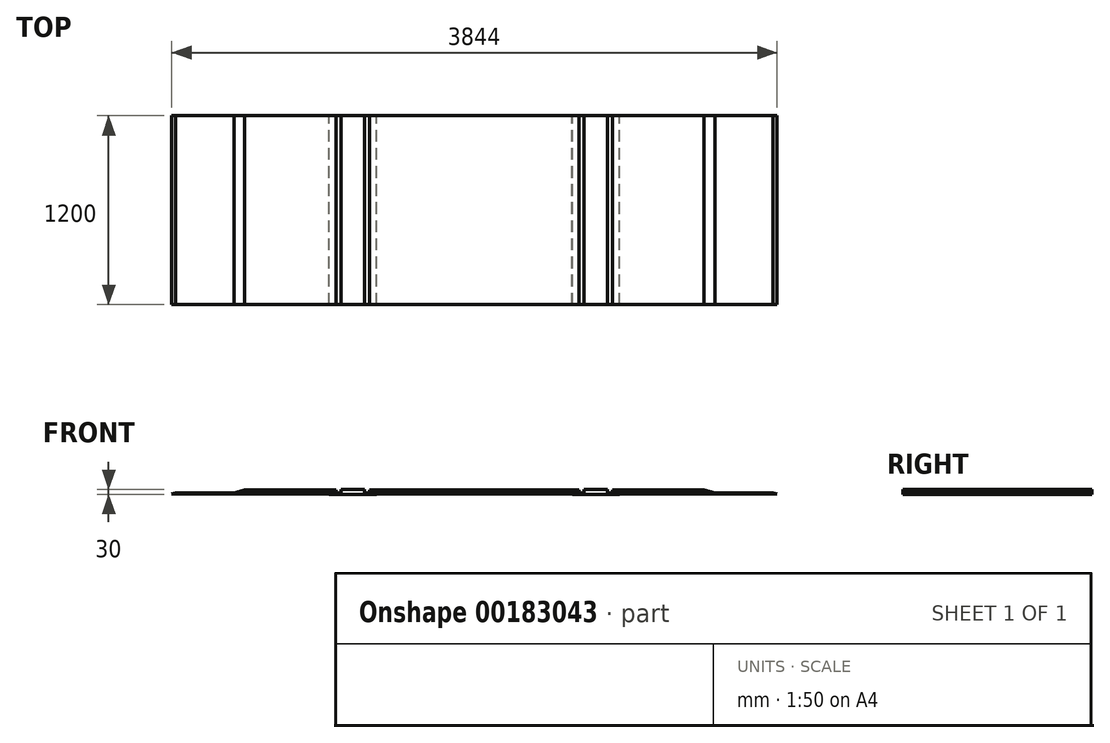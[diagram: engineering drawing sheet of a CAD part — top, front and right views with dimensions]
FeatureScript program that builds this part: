
annotation { "Feature Type Name" : "Feature", "Feature Type Description" : "" }
export const myFeature = defineFeature(function(context is Context, id is Id, definition is map)
    precondition{}
    {
        {
            var Q0;
            Q0=qCreatedBy(makeId("Front.planeOp"),FACE);
            var sketch = newSketch(context, id + "F0", { "sketchPlane" : qUnion([Q0])});
            skLineSegment(sketch, "E0.bottom", {"start": v(-847, 0) * mm, "end": v(-697, 0) * mm});
            skLineSegment(sketch, "E0.top", {"start": v(-847, 20) * mm, "end": v(-697, 20) * mm});
            skLineSegment(sketch, "E0.left", {"start": v(-847, 0) * mm, "end": v(-847, 20) * mm});
            skLineSegment(sketch, "E0.right", {"start": v(-697, 0) * mm, "end": v(-697, 20) * mm});
            skLineSegment(sketch, "E1.bottom", {"start": v(-922, 0) * mm, "end": v(-622, 0) * mm});
            skLineSegment(sketch, "E1.top", {"start": v(-922, -10) * mm, "end": v(-622, -10) * mm});
            skLineSegment(sketch, "E1.left", {"start": v(-922, 0) * mm, "end": v(-922, -10) * mm});
            skLineSegment(sketch, "E1.right", {"start": v(-622, 0) * mm, "end": v(-622, -10) * mm});
            skSolve(sketch);
        }
        {
            var Q0;
            Q0=makeQuery(id+"F0.imprint","IMPRINT",FACE,{"disambiguationData":[TD([[makeQuery(id+"F0.imprint","IMPRINT",EDGE,{"derivedFrom":sQuery(id+"F0.wireOp",EDGE,"E0.top")}),-1.0]])]});
            var Q1;
            Q1=makeQuery(id+"F0.imprint","IMPRINT",FACE,{"disambiguationData":[TD([[makeQuery(id+"F0.imprint","IMPRINT",EDGE,{"derivedFrom":sQuery(id+"F0.wireOp",EDGE,"E1.top")}),1.0]])]});
            extrude(context, id + "F1", {"entities" : qUnion([Q0, Q1]), "endBound" : BoundingType.SYMMETRIC, "depth" : 1200 * mm});
        }
        {
            var Q0;
            Q0=makeQuery(id+"F1.opExtrude","SWEPT_BODY",BODY,{"disambiguationData":[OSD([sQuery(id+"F0.wireOp",EDGE,"E0.top"),sQuery(id+"F0.wireOp",EDGE,"E0.left"),sQuery(id+"F0.wireOp",EDGE,"E0.right"),sQuery(id+"F0.wireOp",EDGE,"E1.bottom"),sQuery(id+"F0.wireOp",EDGE,"E1.top"),sQuery(id+"F0.wireOp",EDGE,"E1.left"),sQuery(id+"F0.wireOp",EDGE,"E1.right")])]});
            var Q1;
            Q1=qCreatedBy(makeId("Right.planeOp"),FACE);
            mirror(context, id + "F2", {"entities" : qUnion([Q0]), "mirrorPlane" : qUnion([Q1])});
        }
        {
            var Q0;
            Q0=qCreatedBy(makeId("Front.planeOp"),FACE);
            var sketch = newSketch(context, id + "F3", { "sketchPlane" : qUnion([Q0])});
            skLineSegment(sketch, "E2", {"start": v(-621, -9) * mm, "end": v(0, -9) * mm});
            skLineSegment(sketch, "E3", {"start": v(0, -9) * mm, "end": v(0, 0) * mm});
            skLineSegment(sketch, "E4", {"start": v(-621, 0) * mm, "end": v(-621, -9) * mm});
            skLineSegment(sketch, "E5.MirrorCS", {"start": v(621, -9) * mm, "end": v(0, -9) * mm});
            skLineSegment(sketch, "E6.MirrorCS", {"start": v(621, 0) * mm, "end": v(621, -9) * mm});
            skLineSegment(sketch, "E7", {"start": v(-621, 0) * mm, "end": v(621, 0) * mm});
            skSolve(sketch);
        }
        {
            var Q0;
            Q0=makeQuery(id+"F3.imprint","IMPRINT",FACE,{"disambiguationData":[TD([[makeQuery(id+"F3.imprint","IMPRINT",EDGE,{"derivedFrom":sQuery(id+"F3.wireOp",EDGE,"E2")}),1.0]])]});
            var Q1;
            {var subQ0=sQuery(id+"F3.wireOp",EDGE,"E3");Q1=makeQuery(id+"F3.imprint","IMPRINT",FACE,{"disambiguationData":[TD([[makeQuery(id+"F3.imprint","IMPRINT",EDGE,{"derivedFrom":subQ0}),-1.0]])]});}
            extrude(context, id + "F4", {"entities" : qUnion([Q0, Q1]), "endBound" : BoundingType.SYMMETRIC, "depth" : 1200 * mm});
        }
        {
            var Q0;
            Q0 = qSketchRegion(id + "F3", true);
            extrude(context, id + "F5", {"entities" : qUnion([Q0]), "endBound" : BoundingType.SYMMETRIC, "depth" : 1200 * mm});
        }
        {
            var Q0;
            Q0=qCreatedBy(makeId("Front.planeOp"),FACE);
            var sketch = newSketch(context, id + "F6", { "sketchPlane" : qUnion([Q0])});
            skLineSegment(sketch, "E8", {"start": v(-922, 0) * mm, "end": v(-1897.27, 0) * mm});
            skLineSegment(sketch, "E9", {"start": v(-1922, -9) * mm, "end": v(-922, -9) * mm});
            skLineSegment(sketch, "E10", {"start": v(-922, -9) * mm, "end": v(-922, 0) * mm});
            skLineSegment(sketch, "E11", {"start": v(-1922, -9) * mm, "end": v(-1897.27, 0) * mm});
            skSolve(sketch);
        }
        {
            var Q0;
            Q0 = qSketchRegion(id + "F6", true);
            extrude(context, id + "F7", {"entities" : qUnion([Q0]), "endBound" : BoundingType.SYMMETRIC, "depth" : 1200 * mm});
        }
        {
            var Q0;
            Q0=qCreatedBy(makeId("Front.planeOp"),FACE);
            var sketch = newSketch(context, id + "F8", { "sketchPlane" : qUnion([Q0])});
            skLineSegment(sketch, "E12", {"start": v(-877, 18) * mm, "end": v(-877, 0) * mm});
            skLineSegment(sketch, "E13", {"start": v(-877, 18) * mm, "end": v(-1459.82, 18) * mm});
            skLineSegment(sketch, "E14", {"start": v(-1459.82, 18) * mm, "end": v(-1527, 0) * mm});
            skLineSegment(sketch, "E15", {"start": v(-1527, 0) * mm, "end": v(-877, 0) * mm});
            skSolve(sketch);
        }
        {
            var Q0;
            Q0=makeQuery(id+"F8.imprint","IMPRINT",FACE,{"disambiguationData":[TD([[makeQuery(id+"F8.imprint","IMPRINT",EDGE,{"derivedFrom":sQuery(id+"F8.wireOp",EDGE,"E12")}),-1.0]])]});
            extrude(context, id + "F9", {"entities" : qUnion([Q0]), "endBound" : BoundingType.SYMMETRIC, "depth" : 1200 * mm});
        }
        {
            var Q0;
            Q0=makeQuery(id+"F9.opExtrude","SWEPT_BODY",BODY,{"disambiguationData":[OSD([sQuery(id+"F8.wireOp",EDGE,"E12"),sQuery(id+"F8.wireOp",EDGE,"E13"),sQuery(id+"F8.wireOp",EDGE,"E14"),sQuery(id+"F8.wireOp",EDGE,"E15")])]});
            var Q1;
            Q1=makeQuery(id+"F7.opExtrude","SWEPT_BODY",BODY,{"disambiguationData":[OSD([sQuery(id+"F6.wireOp",EDGE,"E8"),sQuery(id+"F6.wireOp",EDGE,"E9"),sQuery(id+"F6.wireOp",EDGE,"E10"),sQuery(id+"F6.wireOp",EDGE,"E11")])]});
            var Q2;
            Q2=qCreatedBy(makeId("Right.planeOp"),FACE);
            mirror(context, id + "F10", {"entities" : qUnion([Q0, Q1]), "mirrorPlane" : qUnion([Q2])});
        }
        {
            var Q0;
            Q0=makeQuery(id+"F5.opExtrude","SWEPT_BODY",BODY,{"disambiguationData":[OSD([sQuery(id+"F3.wireOp",EDGE,"IlEzs66W-XQdu-dB0a-ufvr-pwqDSTq3vz9y"),sQuery(id+"F3.wireOp",EDGE,"WTLtitHL-1j3M-uJKV-0gNo-VFhWVUfDdCb5"),sQuery(id+"F3.wireOp",EDGE,"it4Sctpj-h7Bl-NnCC-PNGB-gEzyUDw93y03"),sQuery(id+"F3.wireOp",EDGE,"E2"),sQuery(id+"F3.wireOp",EDGE,"E4"),sQuery(id+"F3.wireOp",EDGE,"43d93d10-b250-4630-8e98-3a0783c7a0780.MirrorCS"),sQuery(id+"F3.wireOp",EDGE,"bd07c16e-2156-4697-9ef1-af36a7aa0dd00.MirrorCS"),sQuery(id+"F3.wireOp",EDGE,"E5.MirrorCS"),sQuery(id+"F3.wireOp",EDGE,"E6.MirrorCS"),sQuery(id+"F3.wireOp",EDGE,"bc8f47d0-8099-4d0b-8b12-18eae32bd22f0.MirrorCS")])]});
            deleteBodies(context, id + "F11", {"entities" : qUnion([Q0])});
        }
        {
            var Q0;
            Q0=qCreatedBy(makeId("Front.planeOp"),FACE);
            var sketch = newSketch(context, id + "F12", { "sketchPlane" : qUnion([Q0])});
            skLineSegment(sketch, "E16.bottom", {"start": v(-665, 0) * mm, "end": v(665, 0) * mm});
            skLineSegment(sketch, "E16.top", {"start": v(-665, 18) * mm, "end": v(665, 18) * mm});
            skLineSegment(sketch, "E16.left", {"start": v(-665, 0) * mm, "end": v(-665, 18) * mm});
            skLineSegment(sketch, "E16.right", {"start": v(665, 0) * mm, "end": v(665, 18) * mm});
            skSolve(sketch);
        }
        {
            var Q0;
            Q0=makeQuery(id+"F12.imprint","IMPRINT",FACE,{"disambiguationData":[TD([[makeQuery(id+"F12.imprint","IMPRINT",EDGE,{"derivedFrom":sQuery(id+"F12.wireOp",EDGE,"E16.bottom")}),1.0]])]});
            extrude(context, id + "F13", {"entities" : qUnion([Q0]), "endBound" : BoundingType.SYMMETRIC, "depth" : 1200 * mm});
        }
    });
